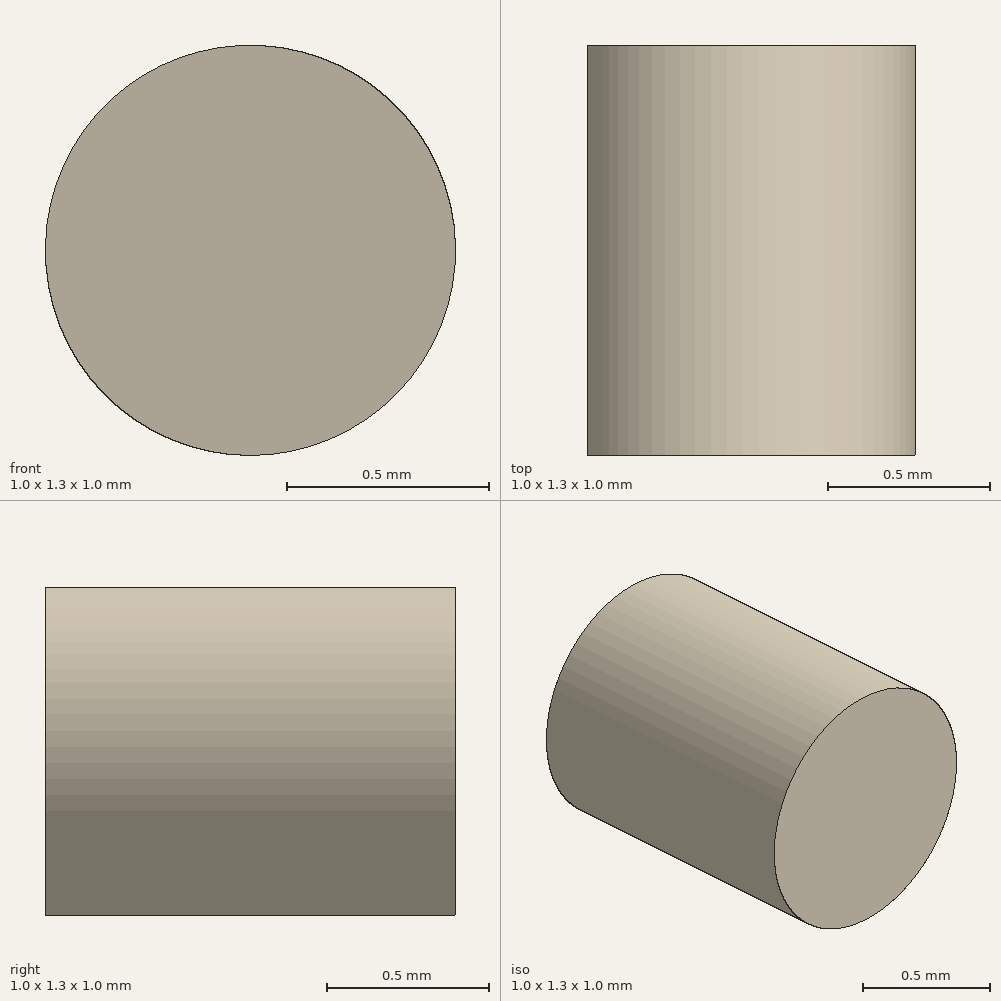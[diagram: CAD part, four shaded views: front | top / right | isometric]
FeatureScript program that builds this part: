
annotation { "Feature Type Name" : "Feature", "Feature Type Description" : "" }
export const myFeature = defineFeature(function(context is Context, id is Id, definition is map)
    precondition{}
    {
        {
            var Q0;
            Q0=qCreatedBy(makeId("Front.planeOp"),FACE);
            var sketch = newSketch(context, id + "F0", { "sketchPlane" : qUnion([Q0])});
            skCircle(sketch, "E0", {"center": v(0, 0) * mm, "radius": 0.5 * mm});
            skLineSegment(sketch, "E1", {"start": v(-0.5, 0) * mm, "end": v(-0.5, -5.08) * mm, "construction": true});
            skLineSegment(sketch, "E2", {"start": v(0, -0.5) * mm, "end": v(-5.08, -0.5) * mm, "construction": true});
            skLineSegment(sketch, "E3", {"start": v(-0.25, -0.18) * mm, "end": v(-0.15, -0.18) * mm});
            skLineSegment(sketch, "E4", {"start": v(0, 0) * mm, "end": v(0, -0.5) * mm});
            skLineSegment(sketch, "E5", {"start": v(0, 0) * mm, "end": v(0, 0.5) * mm});
            skSolve(sketch);
        }
        {
            var Q0;
            Q0=makeQuery(id+"F0.imprint","IMPRINT",FACE,{"disambiguationData":[TD([[makeQuery(id+"F0.imprint","IMPRINT",EDGE,{"derivedFrom":sQuery(id+"F0.wireOp",EDGE,"f318067b-5acd-462f-a804-c0bbfc3c60df")}),1.0]])]});
            var Q1;
            Q1=makeQuery(id+"F0.imprint","IMPRINT",FACE,{"disambiguationData":[TD([[makeQuery(id+"F0.imprint","IMPRINT",EDGE,{"derivedFrom":sQuery(id+"F0.wireOp",EDGE,"b50a9904-7fd8-49d7-ac99-7c6e1697c72b")}),-1.0]])]});
            var Q2;
            {var subQ0=sQuery(id+"F0.wireOp",EDGE,"E4");Q2=makeQuery(id+"F0.imprint","IMPRINT",FACE,{"disambiguationData":[TD([[makeQuery(id+"F0.imprint","IMPRINT",EDGE,{"derivedFrom":subQ0}),1.0]])]});}
            var Q3;
            {var subQ0=sQuery(id+"F0.wireOp",EDGE,"E4");Q3=makeQuery(id+"F0.imprint","IMPRINT",FACE,{"disambiguationData":[TD([[makeQuery(id+"F0.imprint","IMPRINT",EDGE,{"derivedFrom":subQ0}),-1.0]])]});}
            extrude(context, id + "F1", {"entities" : qUnion([Q0, Q1, Q2, Q3]), "depth" : 1.27 * mm});
        }
    });
